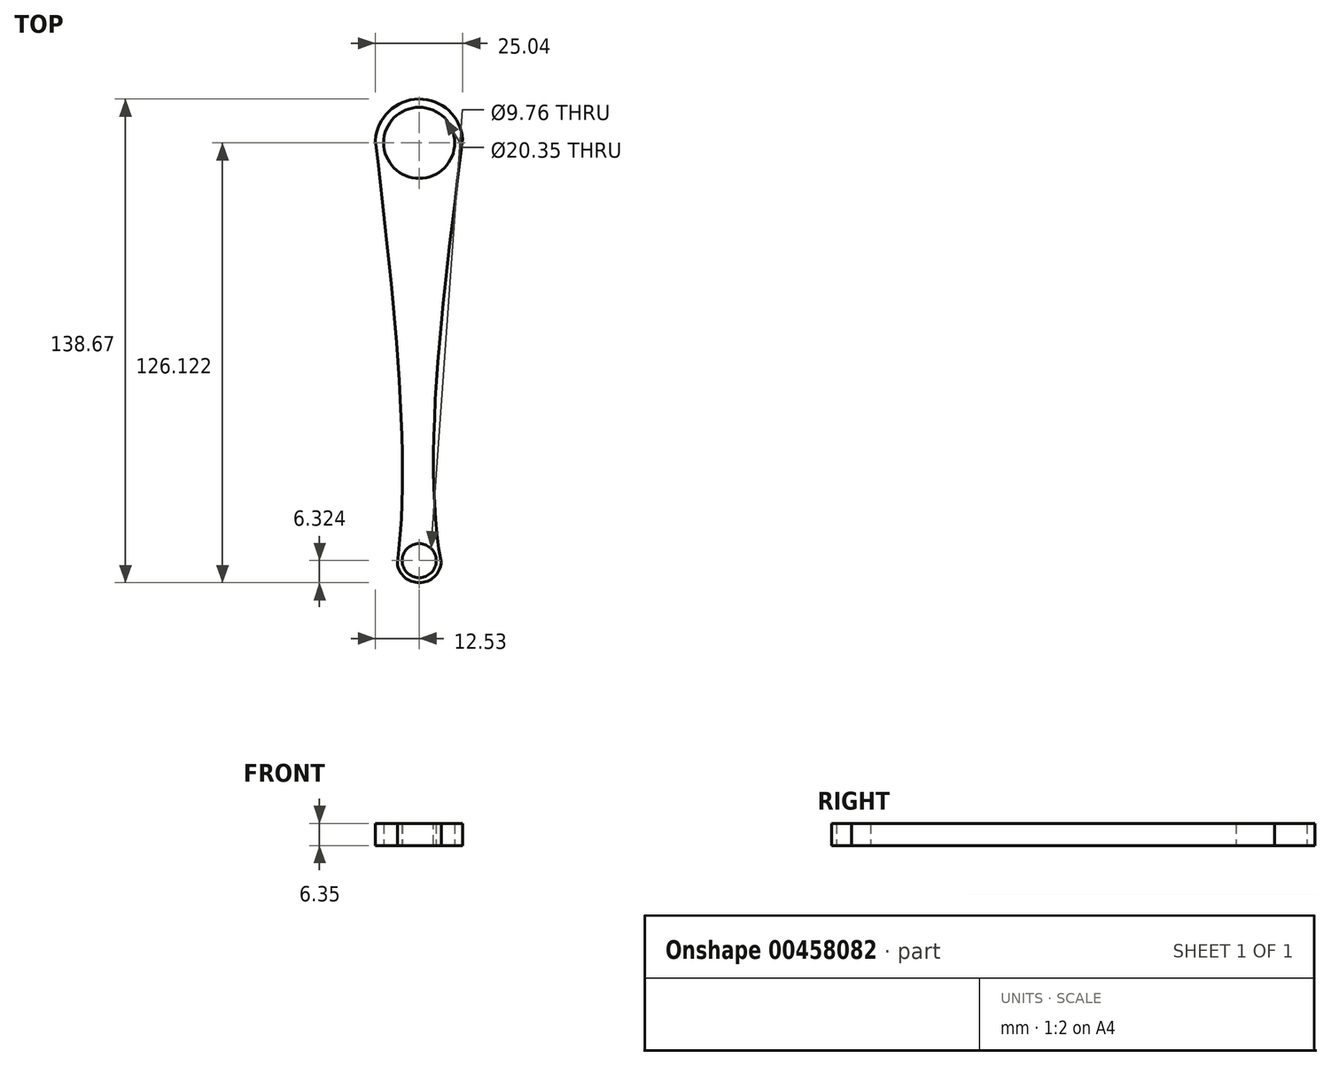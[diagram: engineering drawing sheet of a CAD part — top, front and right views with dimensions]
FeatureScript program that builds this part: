
annotation { "Feature Type Name" : "Feature", "Feature Type Description" : "" }
export const myFeature = defineFeature(function(context is Context, id is Id, definition is map)
    precondition{}
    {
        {
            var Q0;
            Q0=qCreatedBy(makeId("Top.planeOp"),FACE);
            var sketch = newSketch(context, id + "F0", { "sketchPlane" : qUnion([Q0])});
            skArc(sketch, "E0", {"start": v(-6.28, -59.82) * mm, "mid": v(0.06, -65.42) * mm, "end": v(6.3, -59.7) * mm});
            skArc(sketch, "E1", {"start": v(12.5, 61.69) * mm, "mid": v(-0.16, 73.25) * mm, "end": v(-12.53, 61.36) * mm});
            skFitSpline(sketch, "E2", {"points": [v(12.5, 61.69) * mm, v(6.3, -59.7) * mm, v(25.61, -103.78) * mm], "startDerivative": vector(-28.45, -223.43) * mm, "endDerivative": vector(61.5, -97.98) * mm});
            skFitSpline(sketch, "E3", {"points": [v(-12.53, 61.36) * mm, v(-6.28, -59.82) * mm, v(-21.56, -106) * mm], "startDerivative": vector(25.46, -222.03) * mm, "endDerivative": vector(-49.05, -103.84) * mm});
            skCircle(sketch, "E4", {"center": v(0, -59.1) * mm, "radius": 4.88 * mm});
            skCircle(sketch, "E5", {"center": v(0, 60.7) * mm, "radius": 10.18 * mm});
            skSolve(sketch);
        }
        {
            var Q0;
            Q0=makeQuery(id+"F0.imprint","IMPRINT",FACE,{"disambiguationData":[TD([[makeQuery(id+"F0.imprint","IMPRINT",EDGE,{"derivedFrom":sQuery(id+"F0.wireOp",EDGE,"E0")}),1.0]])]});
            extrude(context, id + "F1", {"entities" : qUnion([Q0]), "depth" : 6.35 * mm});
        }
    });
